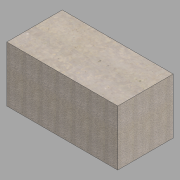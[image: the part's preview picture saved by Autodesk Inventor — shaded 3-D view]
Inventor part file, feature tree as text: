
AUTODESK INVENTOR PART (.ipt)
format: ipt  version: 2022 (Build 260153000, 153)  size: 118,272 bytes
history: native  units: in
note: dims shown in document units (in); Inventor stores cm internally (conversion verified against a paired STEP export)
features: other x1, extrude x1, sketch x1
ambient origin geometry x8: Origin, YZ Plane, XZ Plane, XY Plane, X Axis, Y Axis, Z Axis, Center Point
bodies: Body1 (feature_tree)
feature tree (3):
  other  "Seat wall block"
  extrude  "Extrusion1"  Depth=24.0in
  sketch  "Sketch1"  dims[d0=48.0in d1=24.0in d2=24.0in d3=0.0in]
